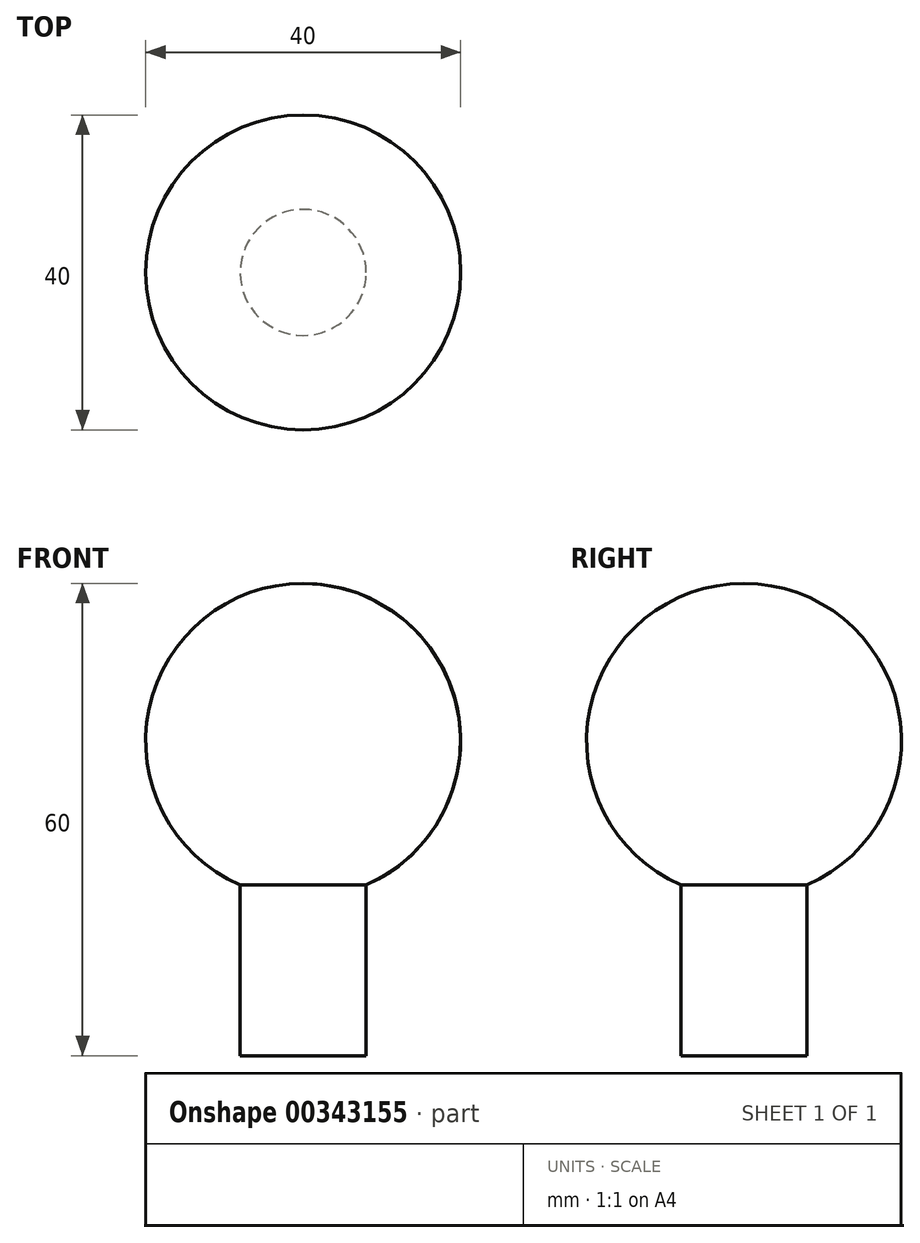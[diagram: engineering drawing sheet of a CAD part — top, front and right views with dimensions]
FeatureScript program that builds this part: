
annotation { "Feature Type Name" : "Feature", "Feature Type Description" : "" }
export const myFeature = defineFeature(function(context is Context, id is Id, definition is map)
    precondition{}
    {
        {
            var Q0;
            Q0=qCreatedBy(makeId("Front.planeOp"),FACE);
            var sketch = newSketch(context, id + "F0", { "sketchPlane" : qUnion([Q0])});
            skArc(sketch, "E0", {"start": v(0, -40) * mm, "mid": v(20, -20) * mm, "end": v(0, 0) * mm});
            skLineSegment(sketch, "E1", {"start": v(0, 0) * mm, "end": v(0, -40) * mm});
            skLineSegment(sketch, "E2", {"start": v(0, -40) * mm, "end": v(0, -60) * mm});
            skLineSegment(sketch, "E3", {"start": v(0, -60) * mm, "end": v(8, -60) * mm});
            skLineSegment(sketch, "E4", {"start": v(8, -60) * mm, "end": v(8, -38.33) * mm});
            skSolve(sketch);
        }
        {
            var Q0;
            Q0 = qSketchRegion(id + "F0", true);
            var Q1;
            Q1=sQuery(id+"F0.wireOp",EDGE,"E1");
            revolve(context, id + "F1", {"entities" : qUnion([Q0]), "axis" : qUnion([Q1]), "revolveType" : RevolveType.FULL});
        }
    });
